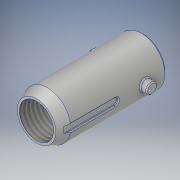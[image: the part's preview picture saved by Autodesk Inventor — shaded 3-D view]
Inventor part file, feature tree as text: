
AUTODESK INVENTOR PART (.ipt)
format: ipt  version: 2019 (Build 230136000, 136)  size: 216,576 bytes
history: native  units: mm
features: other x4, sketch x3, extrude x2, chamfer x2, pattern_circular x1
ambient origin geometry x8: Origin, YZ Plane, XZ Plane, XY Plane, X Axis, Y Axis, Z Axis, Center Point
bodies: Solide1 (feature_tree)
feature tree (12):
  other  "Révolution1"
  other  "Filetage1"
  other  "Plan de construction2"
  extrude  "Extrusion1"  Depth=27.925268mm
  chamfer  "Chanfrein1"  Distance=6.0mm
  pattern_circular  "Réseau circulaire1"  [2 undecoded]
  other  "Plan de construction3"
  extrude  "Extrusion2"  Depth=16.0mm
  chamfer  "Chanfrein3"  Distance=16.0mm
  sketch  "Esquisse1"
  sketch  "Esquisse2"
  sketch  "Esquisse4"
note: 2 required parameter values undecoded (feature->parameter linkage not recoverable at this tier; creation-order binding heuristic only, values carry confidence <= 0.55)
